# Revit family: 634-00-001 DN100-150
name_source: partatom
category: Pipe Accessories
units: mm (PartAtom-declared; Revit-internal decimal feet)

## family parameters
Always vertical = Yes
Cut with Voids When Loaded = No
Part Type = Valve - Breaks Into
Round Connector Dimension = Use Diameter
Shared = No
Work Plane-Based = No

## types (6) — shared parameters
10 = 10 mm  [stored 0.0328084 ft]
2 = 2 mm  [stored 0.00656168 ft]
D2 = 41 mm  [stored 0.134514 ft]
DN100_PN16_AVK ref. no. 634-133-00-016 = 634-133-00-016
DN100_PN16_AVK ref. no. 634-133-00-036 = 634-133-00-036
DN125_PN16_AVK ref. no. 634-161-00-016 = 634-161-00-016
DN125_PN16_AVK ref. no. 634-161-00-036 = 634-161-00-036
DN150_PN16_AVK ref. no. 634-188-00-016 = 634-188-00-016
DN150_PN16_AVK ref. no. 634-188-00-036 = 634-188-00-036
Description_ = AVK SUPA MAXI™ END CAP, PN16
FL_T = 19 mm  [stored 0.062336 ft]
L-L1 = 41 mm  [stored 0.134514 ft]
Search_table = 634-00-001 DN100_150
URL product pages = https://www.avkvalves.com
zero-valued in all types: Default Elevation, Thickness

## per-type parameters (varying)
| type | Bolt_L | Bore | D | D-10 | D1 | D11 | D12 | D1_L | D2_L | DN | L | L1 | Nut | Radius | S1 | S2 |
| DN100_PN16_AVK ref. no. 634-133-00-016 | 68 mm  [stored 0.223097 ft] | 50 mm  [stored 0.164042 ft] | 134 mm | 124 mm  [stored 0.406824 ft] | 77 mm  [stored 0.252625 ft] | 101 mm | 8 mm  [stored 0.0262467 ft] | 54 mm  [stored 0.177165 ft] | 85 mm  [stored 0.278871 ft] | 100 mm  [stored 0.328084 ft] | 115 mm  [stored 0.377297 ft] | 58 mm | 17 mm | 30 mm  [stored 0.0984252 ft] | 52 mm | 67 mm |
| DN100_PN16_AVK ref. no. 634-133-00-036 | 68 mm  [stored 0.223097 ft] | 50 mm  [stored 0.164042 ft] | 134 mm | 124 mm  [stored 0.406824 ft] | 77 mm  [stored 0.252625 ft] | 101 mm | 8 mm  [stored 0.0262467 ft] | 54 mm  [stored 0.177165 ft] | 85 mm  [stored 0.278871 ft] | 100 mm  [stored 0.328084 ft] | 115 mm  [stored 0.377297 ft] | 58 mm | 17 mm | 30 mm  [stored 0.0984252 ft] | 52 mm | 67 mm |
| DN125_PN16_AVK ref. no. 634-161-00-016 | 65 mm  [stored 0.213255 ft] | 63 mm | 143 mm | 133 mm | 92 mm  [stored 0.301837 ft] | 107 mm | 8 mm  [stored 0.0262467 ft] | 64 mm  [stored 0.209974 ft] | 81 mm  [stored 0.265748 ft] | 125 mm | 110 mm  [stored 0.360892 ft] | 55 mm  [stored 0.180446 ft] | 16 mm | 29 mm  [stored 0.0951444 ft] | 66 mm  [stored 0.216535 ft] | 80 mm |
| DN125_PN16_AVK ref. no. 634-161-00-036 | 65 mm  [stored 0.213255 ft] | 63 mm | 143 mm | 133 mm | 92 mm  [stored 0.301837 ft] | 107 mm | 8 mm  [stored 0.0262467 ft] | 64 mm  [stored 0.209974 ft] | 81 mm  [stored 0.265748 ft] | 125 mm | 110 mm  [stored 0.360892 ft] | 55 mm  [stored 0.180446 ft] | 16 mm | 29 mm  [stored 0.0951444 ft] | 66 mm  [stored 0.216535 ft] | 80 mm |
| DN150_PN16_AVK ref. no. 634-188-00-016 | 68 mm  [stored 0.223097 ft] | 75 mm | 170 mm | 160 mm | 105 mm  [stored 0.344488 ft] | 128 mm | 9 mm  [stored 0.0295276 ft] | 64 mm  [stored 0.209974 ft] | 85 mm  [stored 0.278871 ft] | 150 mm | 119 mm  [stored 0.39042 ft] | 60 mm  [stored 0.19685 ft] | 17 mm | 33 mm  [stored 0.108268 ft] | 80 mm | 94 mm  [stored 0.308399 ft] |
| DN150_PN16_AVK ref. no. 634-188-00-036 | 68 mm  [stored 0.223097 ft] | 75 mm | 170 mm | 160 mm | 105 mm  [stored 0.344488 ft] | 128 mm | 10 mm  [stored 0.0328084 ft] | 64 mm  [stored 0.209974 ft] | 85 mm  [stored 0.278871 ft] | 150 mm | 119 mm  [stored 0.39042 ft] | 60 mm  [stored 0.19685 ft] | 17 mm | 35 mm  [stored 0.114829 ft] | 80 mm | 94 mm  [stored 0.308399 ft] |

note: [stored X ft] marks values corroborated as IEEE doubles in the binary element streams (Revit-internal decimal feet)

## geometry (parser evidence)
native form markers: Sweep x5
no freeform markers — native parametric forms only
